# Revit family: EL_Marut_XL
name_source: partatom
category: Lighting Fixtures
units: mm (PartAtom-declared; Revit-internal decimal feet)

## family parameters
Always vertical = Yes
Cut with Voids When Loaded = No
Light Source = Yes
Maintain Annotation Orientation = No
OmniClass Number = 23.80.70.00
OmniClass Title = Lighting
Part Type = Normal
Room Calculation Point = No
Round Connector Dimension = Use Diameter
Shared = No
Work Plane-Based = No

## types (28) — shared parameters
CE Conformity = CE Mark
Certification = ENEC, ENEC+, EMC, Zhaga D4i, IDA
Color Filter = 16777215
Control Gear = LED Driver
Default Elevation = 1500 mm
Description = Street luminaire
Diffuser Material  = Flat glass
Dimming Lamp Color Temperature Shift = <None>
EL_Voltage = AC 220V - 240V / 50-60Hz
Housing Height = 125 mm  [stored 0.410105 ft]
Housing Length = 865 mm  [stored 2.83793 ft]
Housing Width = 455 mm
IK = IK 09 / IK10
IP = IP66
Lamp = LED
Life Time = 120 000 h
Light Source Symbol Length = 3048 mm  [stored 10 ft]
Luminaire Material = Kov
Luminaire Type = MARUT XL G2
Manufacturer = ELEKTRO-LUMEN, s. r. o.
Model = MARUT XL G2
Spot Beam Angle = 30.00°
Spot Field Angle = 90.00°
Terminal Block Poles = 2, 3, 5
Tilt Angle = 90.00°
URL Luminaire = https://www.el-lumen.cz
URL Manufacturer = https://www.el-lumen.cz
Voltage  = AC 220V - 240V / 50-60Hz
Weight = 15.2

## per-type parameters (varying)
| type | CCT | CRI | Luminous Flux of LED | Luminous Flux of Luminaire | Optic | Optical Efficacy | Power |
| MARUT XL G2 Mxx 30k0 740 | 4000 | 70 | 30000 lm | 26007 lm | M03 | 86.69 | 173 W |
| MARUT XL G2 Mxx 28k0 740 | 4000 | 70 | 28000 lm | 24273 lm | M03 | 86.69 | 160 W |
| MARUT XL G2 Mxx 24k0 740 | 4000 | 70 | 24000 lm | 20806 lm | M03 | 86.69 | 143 W |
| MARUT XL G2 Mxx 21k0 740 | 4000 | 70 | 21000 lm | 18205 lm | M03 | 86.69 | 123 W |
| MARUT XL G2 Mxx 18k0 740 | 4000 | 70 | 18000 lm | 15604 lm | M03 | 86.69 | 108 W |
| MARUT XL G2 Mxx 16k0 740 | 4000 | 70 | 16000 lm | 13870 lm | M03 | 86.69 | 94 W |
| MARUT XL G2 Mxx 14k0 740 | 4000 | 70 | 14000 lm | 12137 lm | M03 | 86.69 | 81 W |
| MARUT XL G2 Mxx 28k0 730 | 3000 | 70 | 28000 lm | 24273 lm | M03 | 86.69 | 169 W |
| MARUT XL G2 Mxx 24k0 730 | 3000 | 70 | 24000 lm | 20806 lm | M03 | 86.69 | 152 W |
| MARUT XL G2 Mxx 21k0 730 | 3000 | 70 | 21000 lm | 18205 lm | M03 | 86.69 | 129 W |
| MARUT XL G2 Mxx 18k0 730 | 3000 | 70 | 18000 lm | 15604 lm | M03 | 86.69 | 116 W |
| MARUT XL G2 Mxx 16k0 730 | 3000 | 70 | 16000 lm | 13870 lm | M03 | 86.69 | 100 W |
| MARUT XL G2 Mxx 14k0 730 | 3000 | 70 | 14000 lm | 12137 lm | M03 | 86.69 | 86 W |
| MARUT XL G2 Mxx 24k0 727 | 2700 | 70 | 24000 lm | 20806 lm | M03 | 86.69 | 150 W |
| MARUT XL G2 Mxx 21k0 727 | 2700 | 70 | 21000 lm | 18205 lm | M03 | 86.69 | 138 W |
| MARUT XL G2 Mxx 18k0 727 | 2700 | 70 | 18000 lm | 15604 lm | M03 | 86.69 | 117 W |
| MARUT XL G2 Mxx 16k0 727 | 2700 | 70 | 16000 lm | 13870 lm | M03 | 86.69 | 101 W |
| MARUT XL G2 Mxx 14k0 727 | 2700 | 70 | 14000 lm | 12137 lm | M03 | 86.69 | 91 W |
| MARUT XL G2 Mxx 24k0 722 | 2200 | 70 | 24000 lm | 20806 lm | M03 | 86.69 | 175 W |
| MARUT XL G2 Mxx 21k0 722 | 2200 | 70 | 21000 lm | 18205 lm | M03 | 86.69 | 149 W |
| MARUT XL G2 Mxx 18k0 722 | 2200 | 70 | 18000 lm | 15604 lm | M03 | 86.69 | 134 W |
| MARUT XL G2 Mxx 16k0 722 | 2200 | 70 | 16000 lm | 13870 lm | M03 | 86.69 | 118 W |
| MARUT XL G2 Mxx 14k0 722 | 2200 | 70 | 14000 lm | 12137 lm | M03 | 86.69 | 101 W |
| MARUT XL G2 Lxx 24k0 AMB | 1850 | 50 | 24000 lm | 21677 lm | L03 | 90.32 | 158 W |
| MARUT XL G2 Lxx 21k0 AMB | 1850 | 50 | 21000 lm | 18967 lm | L03 | 90.32 | 138 W |
| MARUT XL G2 Lxx 18k0 AMB | 1850 | 50 | 18000 lm | 16258 lm | L03 | 90.32 | 122 W |
| MARUT XL G2 Lxx 16k0 AMB | 1850 | 50 | 16000 lm | 14451 lm | L03 | 90.32 | 107 W |
| MARUT XL G2 Lxx 14k0 AMB | 1850 | 50 | 14000 lm | 12645 lm | L03 | 90.32 | 92 W |

note: column(s) folded — value = type name in every type: Luminaire Model

note: [stored X ft] marks values corroborated as IEEE doubles in the binary element streams (Revit-internal decimal feet)
